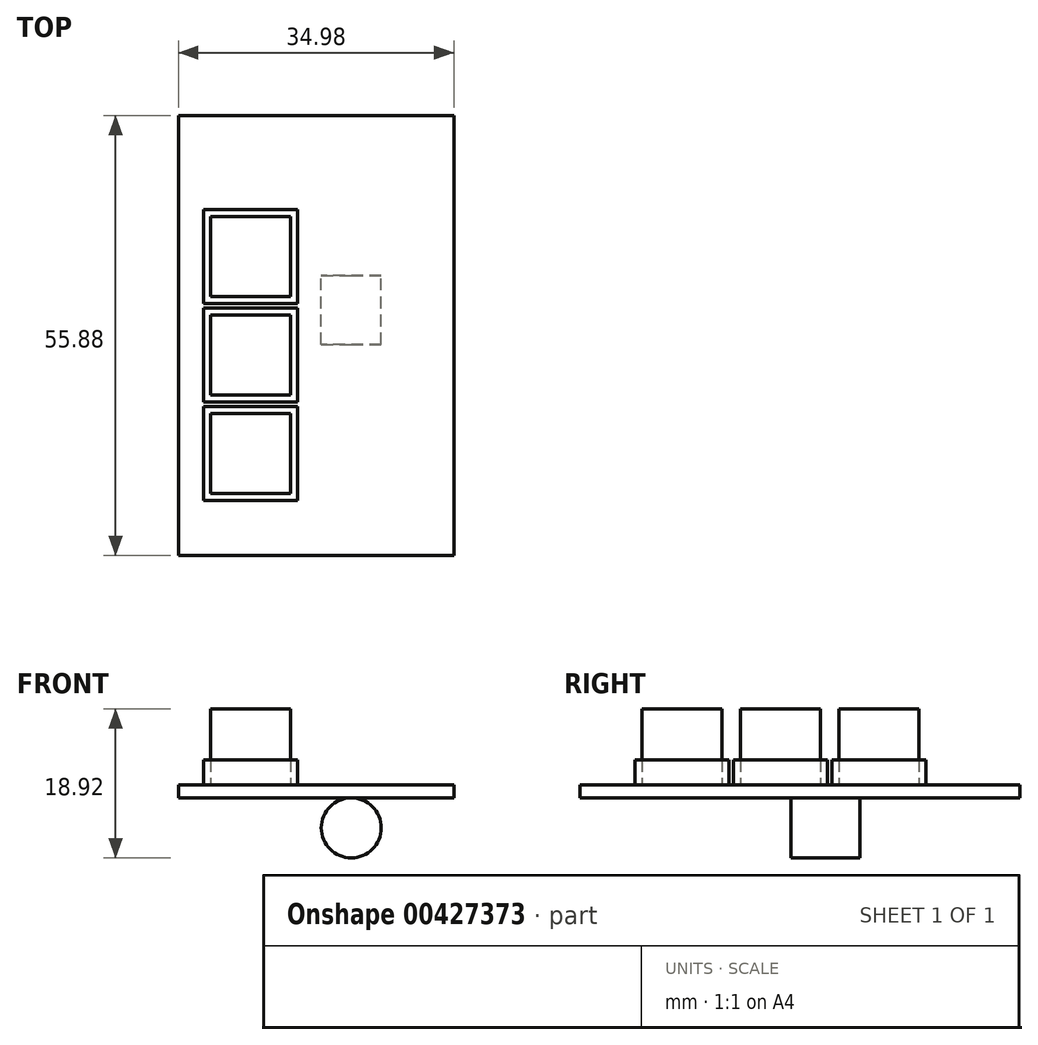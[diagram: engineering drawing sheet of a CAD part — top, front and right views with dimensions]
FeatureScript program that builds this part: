
annotation { "Feature Type Name" : "Feature", "Feature Type Description" : "" }
export const myFeature = defineFeature(function(context is Context, id is Id, definition is map)
    precondition{}
    {
        {
            var Q0;
            Q0=qCreatedBy(makeId("Top.planeOp"),FACE);
            var sketch = newSketch(context, id + "F0", { "sketchPlane" : qUnion([Q0])});
            skLineSegment(sketch, "E0.bottom", {"start": v(0, 0) * mm, "end": v(34.98, 0) * mm});
            skLineSegment(sketch, "E0.top", {"start": v(0, -55.88) * mm, "end": v(34.98, -55.88) * mm});
            skLineSegment(sketch, "E0.left", {"start": v(0, 0) * mm, "end": v(0, -55.88) * mm});
            skLineSegment(sketch, "E0.right", {"start": v(34.98, 0) * mm, "end": v(34.98, -55.88) * mm});
            skLineSegment(sketch, "E1.bottom", {"start": v(3.18, -36.96) * mm, "end": v(15.11, -36.96) * mm});
            skLineSegment(sketch, "E1.top", {"start": v(3.18, -48.9) * mm, "end": v(15.11, -48.9) * mm});
            skLineSegment(sketch, "E1.left", {"start": v(3.18, -36.96) * mm, "end": v(3.18, -48.9) * mm});
            skLineSegment(sketch, "E1.right", {"start": v(15.11, -36.96) * mm, "end": v(15.11, -48.9) * mm});
            skLineSegment(sketch, "E2", {"start": v(3.17, 0) * mm, "end": v(3.17, -55.88) * mm, "construction": true});
            skLineSegment(sketch, "E3", {"start": v(0, -48.9) * mm, "end": v(34.98, -48.9) * mm, "construction": true});
            skLineSegment(sketch, "E4.bottom", {"start": v(3.18, -24.45) * mm, "end": v(15.11, -24.45) * mm});
            skLineSegment(sketch, "E4.right", {"start": v(15.11, -24.45) * mm, "end": v(15.11, -36.39) * mm});
            skLineSegment(sketch, "E5.bottom", {"start": v(3.18, -11.94) * mm, "end": v(15.11, -11.94) * mm});
            skLineSegment(sketch, "E5.top", {"start": v(3.18, -23.88) * mm, "end": v(15.11, -23.88) * mm});
            skLineSegment(sketch, "E5.left", {"start": v(3.17, -11.94) * mm, "end": v(3.17, -23.88) * mm});
            skLineSegment(sketch, "E5.right", {"start": v(15.11, -11.94) * mm, "end": v(15.11, -23.88) * mm});
            skLineSegment(sketch, "E6", {"start": v(15.11, -36.39) * mm, "end": v(3.17, -36.39) * mm});
            skLineSegment(sketch, "E7", {"start": v(3.17, -36.39) * mm, "end": v(3.18, -24.45) * mm});
            skLineSegment(sketch, "E8", {"start": v(9.14, -23.88) * mm, "end": v(9.14, -36.96) * mm, "construction": true});
            skLineSegment(sketch, "E9", {"start": v(3.18, -24.45) * mm, "end": v(15.11, -36.39) * mm, "construction": true});
            skPoint(sketch, "E10", {"position": v(9.14, -30.42) * mm});
            skLineSegment(sketch, "E11", {"start": v(3.18, -36.96) * mm, "end": v(15.11, -48.9) * mm, "construction": true});
            skLineSegment(sketch, "E12", {"start": v(15.11, -36.96) * mm, "end": v(3.18, -48.9) * mm, "construction": true});
            skLineSegment(sketch, "E13", {"start": v(15.11, -24.45) * mm, "end": v(3.17, -36.39) * mm, "construction": true});
            skLineSegment(sketch, "E14", {"start": v(15.11, -23.88) * mm, "end": v(3.18, -11.94) * mm, "construction": true});
            skLineSegment(sketch, "E15", {"start": v(15.11, -11.94) * mm, "end": v(3.18, -23.88) * mm, "construction": true});
            skLineSegment(sketch, "E16.bottom", {"start": v(4.06, -37.85) * mm, "end": v(14.22, -37.85) * mm});
            skLineSegment(sketch, "E16.top", {"start": v(4.06, -48) * mm, "end": v(14.22, -48) * mm});
            skLineSegment(sketch, "E16.left", {"start": v(4.06, -37.85) * mm, "end": v(4.06, -48) * mm});
            skLineSegment(sketch, "E16.right", {"start": v(14.22, -37.85) * mm, "end": v(14.22, -48) * mm});
            skLineSegment(sketch, "E17", {"start": v(4.06, -37.85) * mm, "end": v(14.22, -48) * mm, "construction": true});
            skLineSegment(sketch, "E18", {"start": v(14.22, -37.85) * mm, "end": v(4.06, -48) * mm, "construction": true});
            skPoint(sketch, "E19", {"position": v(9.14, -42.93) * mm});
            skLineSegment(sketch, "E20.bottom", {"start": v(4.06, -12.83) * mm, "end": v(14.22, -12.83) * mm});
            skLineSegment(sketch, "E20.top", {"start": v(4.06, -22.99) * mm, "end": v(14.22, -22.99) * mm});
            skLineSegment(sketch, "E20.left", {"start": v(4.06, -12.83) * mm, "end": v(4.06, -22.99) * mm});
            skLineSegment(sketch, "E20.right", {"start": v(14.22, -12.83) * mm, "end": v(14.22, -22.99) * mm});
            skLineSegment(sketch, "E21", {"start": v(4.06, -12.83) * mm, "end": v(14.22, -22.99) * mm, "construction": true});
            skLineSegment(sketch, "E22", {"start": v(14.22, -12.83) * mm, "end": v(4.06, -22.99) * mm, "construction": true});
            skPoint(sketch, "E23", {"position": v(9.14, -17.9) * mm});
            skLineSegment(sketch, "E24.bottom", {"start": v(4.06, -25.34) * mm, "end": v(14.22, -25.34) * mm});
            skLineSegment(sketch, "E24.top", {"start": v(4.06, -35.5) * mm, "end": v(14.22, -35.5) * mm});
            skLineSegment(sketch, "E24.left", {"start": v(4.06, -25.34) * mm, "end": v(4.06, -35.5) * mm});
            skLineSegment(sketch, "E24.right", {"start": v(14.22, -25.34) * mm, "end": v(14.22, -35.5) * mm});
            skLineSegment(sketch, "E25", {"start": v(4.06, -25.34) * mm, "end": v(14.22, -35.5) * mm, "construction": true});
            skLineSegment(sketch, "E26", {"start": v(14.22, -25.34) * mm, "end": v(4.06, -35.5) * mm, "construction": true});
            skSolve(sketch);
        }
        {
            var Q0;
            Q0=makeQuery(id+"F0.imprint","IMPRINT",FACE,{"disambiguationData":[TD([[makeQuery(id+"F0.imprint","IMPRINT",EDGE,{"derivedFrom":sQuery(id+"F0.wireOp",EDGE,"E0.bottom")}),-1.0]])]});
            var Q1;
            Q1=makeQuery(id+"F0.imprint","IMPRINT",FACE,{"disambiguationData":[TD([[makeQuery(id+"F0.imprint","IMPRINT",EDGE,{"derivedFrom":sQuery(id+"F0.wireOp",EDGE,"E1.bottom")}),-1.0]])]});
            var Q2;
            Q2=makeQuery(id+"F0.imprint","IMPRINT",FACE,{"disambiguationData":[TD([[makeQuery(id+"F0.imprint","IMPRINT",EDGE,{"derivedFrom":sQuery(id+"F0.wireOp",EDGE,"E24.bottom")}),-1.0]])]});
            var Q3;
            Q3=makeQuery(id+"F0.imprint","IMPRINT",FACE,{"disambiguationData":[TD([[makeQuery(id+"F0.imprint","IMPRINT",EDGE,{"derivedFrom":sQuery(id+"F0.wireOp",EDGE,"E20.bottom")}),-1.0]])]});
            var Q4;
            Q4=makeQuery(id+"F0.imprint","IMPRINT",FACE,{"disambiguationData":[TD([[makeQuery(id+"F0.imprint","IMPRINT",EDGE,{"derivedFrom":sQuery(id+"F0.wireOp",EDGE,"E5.bottom")}),-1.0]])]});
            var Q5;
            Q5=makeQuery(id+"F0.imprint","IMPRINT",FACE,{"disambiguationData":[TD([[makeQuery(id+"F0.imprint","IMPRINT",EDGE,{"derivedFrom":sQuery(id+"F0.wireOp",EDGE,"E16.bottom")}),-1.0]])]});
            var Q6;
            Q6=makeQuery(id+"F0.imprint","IMPRINT",FACE,{"disambiguationData":[TD([[makeQuery(id+"F0.imprint","IMPRINT",EDGE,{"derivedFrom":sQuery(id+"F0.wireOp",EDGE,"E4.bottom")}),-1.0]])]});
            extrude(context, id + "F1", {"entities" : qUnion([Q0, Q1, Q2, Q3, Q4, Q5, Q6]), "oppositeDirection" : true, "depth" : 1.65 * mm, "offsetDistance" : 25.4 * mm});
        }
        {
            var Q0;
            Q0=makeQuery(id+"F0.imprint","IMPRINT",FACE,{"disambiguationData":[TD([[makeQuery(id+"F0.imprint","IMPRINT",EDGE,{"derivedFrom":sQuery(id+"F0.wireOp",EDGE,"E5.bottom")}),-1.0]])]});
            var Q1;
            Q1=makeQuery(id+"F0.imprint","IMPRINT",FACE,{"disambiguationData":[TD([[makeQuery(id+"F0.imprint","IMPRINT",EDGE,{"derivedFrom":sQuery(id+"F0.wireOp",EDGE,"E20.bottom")}),-1.0]])]});
            var Q2;
            Q2=makeQuery(id+"F0.imprint","IMPRINT",FACE,{"disambiguationData":[TD([[makeQuery(id+"F0.imprint","IMPRINT",EDGE,{"derivedFrom":sQuery(id+"F0.wireOp",EDGE,"E4.bottom")}),-1.0]])]});
            var Q3;
            Q3=makeQuery(id+"F0.imprint","IMPRINT",FACE,{"disambiguationData":[TD([[makeQuery(id+"F0.imprint","IMPRINT",EDGE,{"derivedFrom":sQuery(id+"F0.wireOp",EDGE,"E24.bottom")}),-1.0]])]});
            var Q4;
            Q4=makeQuery(id+"F0.imprint","IMPRINT",FACE,{"disambiguationData":[TD([[makeQuery(id+"F0.imprint","IMPRINT",EDGE,{"derivedFrom":sQuery(id+"F0.wireOp",EDGE,"E1.bottom")}),-1.0]])]});
            var Q5;
            Q5=makeQuery(id+"F0.imprint","IMPRINT",FACE,{"disambiguationData":[TD([[makeQuery(id+"F0.imprint","IMPRINT",EDGE,{"derivedFrom":sQuery(id+"F0.wireOp",EDGE,"E16.bottom")}),-1.0]])]});
            extrude(context, id + "F2", {"entities" : qUnion([Q0, Q1, Q2, Q3, Q4, Q5]), "depth" : 3.17 * mm, "offsetDistance" : 25.4 * mm});
        }
        {
            var Q0;
            Q0=makeQuery(id+"F0.imprint","IMPRINT",FACE,{"disambiguationData":[TD([[makeQuery(id+"F0.imprint","IMPRINT",EDGE,{"derivedFrom":sQuery(id+"F0.wireOp",EDGE,"E20.bottom")}),-1.0]])]});
            var Q1;
            Q1=makeQuery(id+"F0.imprint","IMPRINT",FACE,{"disambiguationData":[TD([[makeQuery(id+"F0.imprint","IMPRINT",EDGE,{"derivedFrom":sQuery(id+"F0.wireOp",EDGE,"E24.bottom")}),-1.0]])]});
            var Q2;
            Q2=makeQuery(id+"F0.imprint","IMPRINT",FACE,{"disambiguationData":[TD([[makeQuery(id+"F0.imprint","IMPRINT",EDGE,{"derivedFrom":sQuery(id+"F0.wireOp",EDGE,"E16.bottom")}),-1.0]])]});
            extrude(context, id + "F3", {"entities" : qUnion([Q0, Q1, Q2]), "depth" : 9.65 * mm, "offsetDistance" : 25.4 * mm});
        }
        {
            var Q0;
            Q0=qCreatedBy(makeId("Front.planeOp"),FACE);
            cPlane(context, id + "F4", {"entities" : qUnion([Q0]), "cplaneType" : CPlaneType.OFFSET, "offset" : 20.32 * mm, "width" : 152.4 * mm, "height" : 152.4 * mm});
        }
        {
            var Q0;
            Q0=qCreatedBy(id+"F4.planeOp",FACE);
            var sketch = newSketch(context, id + "F5", { "sketchPlane" : qUnion([Q0])});
            skCircle(sketch, "E27", {"center": v(21.94, -5.46) * mm, "radius": 3.81 * mm});
            skSolve(sketch);
        }
        {
            var Q0;
            Q0=makeQuery(id+"F5.imprint","IMPRINT",FACE,{"disambiguationData":[TD([[makeQuery(id+"F5.imprint","IMPRINT",EDGE,{"derivedFrom":sQuery(id+"F5.wireOp",EDGE,"E27")}),1.0]])]});
            extrude(context, id + "F6", {"entities" : qUnion([Q0]), "operationType" : NewBodyOperationType.ADD, "depth" : 8.76 * mm, "offsetDistance" : 25.4 * mm});
        }
    });
